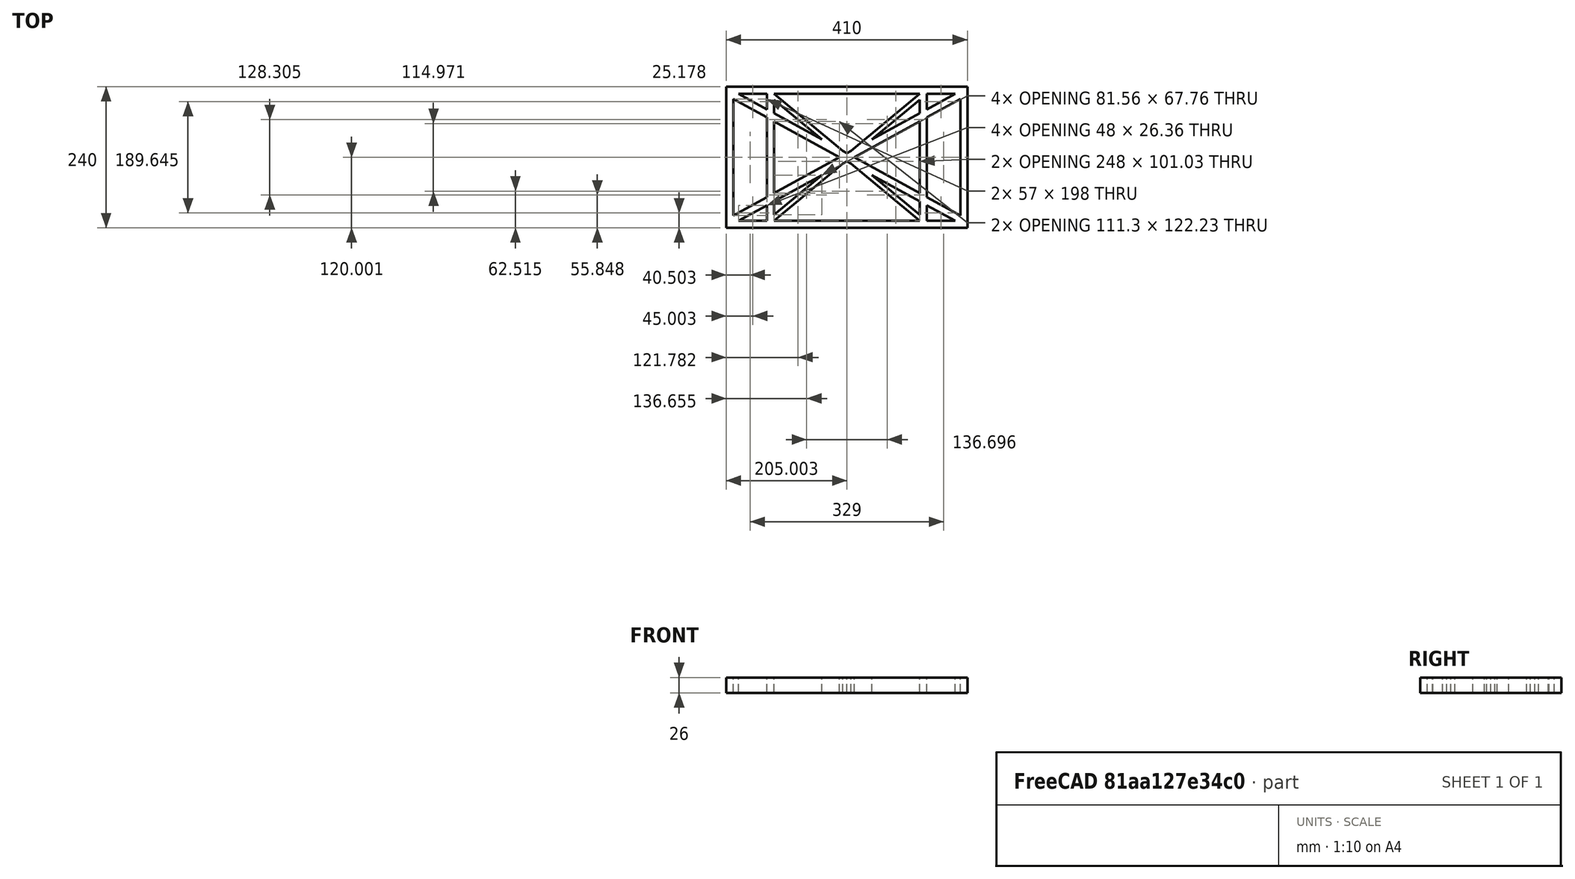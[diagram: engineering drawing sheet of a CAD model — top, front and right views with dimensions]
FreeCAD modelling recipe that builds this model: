
FCSTD DOCUMENT  (FreeCAD 0.19R0.19.2)
Label: laptopStand031
License: All rights reserved
LicenseURL: http://en.wikipedia.org/wiki/All_rights_reserved
objects: Sketcher::SketchObject×3, Part::Extrusion×1
note: 4 computed .brp shape members not serialized (recipe doc carries the construction recipe); baked Part::Feature solids carry a one-line shape summary decoded from their .brp

FEATURE [Sketcher::SketchObject] Sketch
  FullyConstrained = true
  sketch-geometry (52):
    g0: LineSegment StartX=-22.9272 StartY=136.221 StartZ=0 EndX=-22.9272 EndY=-103.779 EndZ=0
    g1: LineSegment StartX=-22.9272 StartY=136.221 StartZ=0 EndX=387.073 EndY=136.221 EndZ=0
    g2: LineSegment StartX=-22.9272 StartY=-103.779 StartZ=0 EndX=387.073 EndY=-103.779 EndZ=0
    g3: LineSegment StartX=387.073 StartY=136.221 StartZ=0 EndX=387.073 EndY=-103.779 EndZ=0
    g4: LineSegment StartX=375.073 StartY=115.221 StartZ=0 EndX=318.073 EndY=83.9235 EndZ=0
    g5: LineSegment StartX=-10.9272 StartY=-82.7794 StartZ=0 EndX=46.0728 EndY=-51.4823 EndZ=0
    g6: LineSegment StartX=-1.92719 StartY=124.221 StartZ=0 EndX=46.0728 EndY=97.8651 EndZ=0
    g7: LineSegment StartX=366.073 StartY=-91.7794 StartZ=0 EndX=318.073 EndY=-65.424 EndZ=0
    g8: LineSegment StartX=-10.9272 StartY=115.221 StartZ=0 EndX=-10.9272 EndY=-82.7794 EndZ=0
    g9: LineSegment StartX=375.073 StartY=-82.7794 StartZ=0 EndX=375.073 EndY=115.221 EndZ=0
    g10: LineSegment StartX=-1.92719 StartY=-91.7794 StartZ=0 EndX=46.0728 EndY=-91.7794 EndZ=0
    g11: LineSegment StartX=318.073 StartY=124.221 StartZ=0 EndX=366.073 EndY=124.221 EndZ=0
    g12: LineSegment StartX=306.073 StartY=-81.8102 StartZ=0 EndX=224.513 EndY=-14.0532 EndZ=0
    g13: LineSegment StartX=58.0728 StartY=114.251 StartZ=0 EndX=139.632 EndY=46.4944 EndZ=0
    g14: LineSegment StartX=306.073 StartY=124.221 StartZ=0 EndX=189.124 EndY=27.0628 EndZ=0
    g15: LineSegment StartX=58.0728 StartY=-91.7794 StartZ=0 EndX=175.022 EndY=5.37834 EndZ=0
    g16: LineSegment StartX=46.0728 StartY=124.221 StartZ=0 EndX=46.0728 EndY=97.8651 EndZ=0
    g17: LineSegment StartX=58.0728 StartY=-81.8102 StartZ=0 EndX=58.0728 EndY=-58.8351 EndZ=0
    g18: LineSegment StartX=318.073 StartY=124.221 StartZ=0 EndX=318.073 EndY=97.8651 EndZ=0
    g19: LineSegment StartX=306.073 StartY=114.251 StartZ=0 EndX=306.073 EndY=91.2763 EndZ=0
    g20: LineSegment StartX=182.073 StartY=23.1914 StartZ=0 EndX=189.124 EndY=27.0628 EndZ=0
    g21: LineSegment StartX=182.073 StartY=9.24976 StartZ=0 EndX=175.022 EndY=5.37834 EndZ=0
    g22: LineSegment StartX=224.513 StartY=46.4944 StartZ=0 EndX=306.073 EndY=114.251 EndZ=0
    g23: LineSegment StartX=175.022 StartY=27.0628 StartZ=0 EndX=58.0728 EndY=124.221 EndZ=0
    g24: LineSegment StartX=169.377 StartY=16.2206 StartZ=0 EndX=58.0728 EndY=77.3346 EndZ=0
    g25: LineSegment StartX=139.632 StartY=-14.0532 StartZ=0 EndX=58.0728 EndY=-81.8102 EndZ=0
    g26: LineSegment StartX=194.768 StartY=16.2206 StartZ=0 EndX=306.073 EndY=-44.8935 EndZ=0
    g27: LineSegment StartX=224.513 StartY=46.4944 StartZ=0 EndX=306.073 EndY=91.2763 EndZ=0
    g28: LineSegment StartX=175.022 StartY=27.0628 StartZ=0 EndX=182.073 EndY=23.1914 EndZ=0
    g29: LineSegment StartX=139.632 StartY=-14.0532 StartZ=0 EndX=58.0728 EndY=-58.8351 EndZ=0
    g30: LineSegment StartX=189.124 StartY=5.37834 StartZ=0 EndX=182.073 EndY=9.24976 EndZ=0
    g31: LineSegment StartX=189.124 StartY=5.37834 StartZ=0 EndX=306.073 EndY=-91.7794 EndZ=0
    g32: LineSegment StartX=306.073 StartY=77.3346 StartZ=0 EndX=306.073 EndY=-44.8935 EndZ=0
    g33: LineSegment StartX=318.073 StartY=83.9235 StartZ=0 EndX=318.073 EndY=-51.4823 EndZ=0
    g34: LineSegment StartX=318.073 StartY=97.8651 StartZ=0 EndX=366.073 EndY=124.221 EndZ=0
    g35: LineSegment StartX=306.073 StartY=77.3346 StartZ=0 EndX=194.768 EndY=16.2206 EndZ=0
    g36: LineSegment StartX=306.073 StartY=-58.8351 StartZ=0 EndX=224.513 EndY=-14.0532 EndZ=0
    g37: LineSegment StartX=306.073 StartY=-58.8351 StartZ=0 EndX=306.073 EndY=-81.8102 EndZ=0
    g38: LineSegment StartX=318.073 StartY=-51.4823 StartZ=0 EndX=375.073 EndY=-82.7794 EndZ=0
    g39: LineSegment StartX=318.073 StartY=-65.424 StartZ=0 EndX=318.073 EndY=-91.7794 EndZ=0
    g40: LineSegment StartX=306.073 StartY=124.221 StartZ=0 EndX=58.0728 EndY=124.221 EndZ=0
    g41: LineSegment StartX=318.073 StartY=-91.7794 StartZ=0 EndX=366.073 EndY=-91.7794 EndZ=0
    g42: LineSegment StartX=58.0728 StartY=-91.7794 StartZ=0 EndX=306.073 EndY=-91.7794 EndZ=0
    g43: LineSegment StartX=58.0728 StartY=-44.8935 StartZ=0 EndX=58.0728 EndY=77.3346 EndZ=0
    g44: LineSegment StartX=46.0728 StartY=-65.424 StartZ=0 EndX=-1.92719 EndY=-91.7794 EndZ=0
    g45: LineSegment StartX=46.0728 StartY=-65.424 StartZ=0 EndX=46.0728 EndY=-91.7794 EndZ=0
    g46: LineSegment StartX=58.0728 StartY=-44.8935 StartZ=0 EndX=169.377 EndY=16.2206 EndZ=0
    g47: LineSegment StartX=58.0728 StartY=91.2763 StartZ=0 EndX=58.0728 EndY=114.251 EndZ=0
    g48: LineSegment StartX=46.0728 StartY=83.9235 StartZ=0 EndX=46.0728 EndY=-51.4823 EndZ=0
    g49: LineSegment StartX=46.0728 StartY=124.221 StartZ=0 EndX=-1.92719 EndY=124.221 EndZ=0
    g50: LineSegment StartX=58.0728 StartY=91.2763 StartZ=0 EndX=139.632 EndY=46.4944 EndZ=0
    g51: LineSegment StartX=46.0728 StartY=83.9235 StartZ=0 EndX=-10.9272 EndY=115.221 EndZ=0
  constraints (102):
    c: Vertical(g0)
    c: Distance(g0) = 240
    c: Horizontal(g1)
    c: Distance(g1) = 410
    c: Coincident(g1,g0)
    c: Coincident(g2,g0)
    c: Horizontal(g2)
    c: Coincident(g3,g1)
    c: Vertical(g3)
    c: Coincident(g2,g3)
    c: Block(g1)
    c: Horizontal(g10)
    c: Horizontal(g11)
    c: PointOnObject(g35,g6)
    c: Coincident(g28,g20)
    c: Coincident(g30,g21)
    c: Tangent(g7,g24)
    c: PointOnObject(g24,g5)
    c: PointOnObject(g26,g4)
    c: Coincident(g20,g14)
    c: Tangent(g20,g27)
    c: Coincident(g50,g13)
    c: Coincident(g28,g23)
    c: Coincident(g22,g27)
    c: Coincident(g21,g15)
    c: Coincident(g29,g25)
    c: Tangent(g21,g29)
    c: Coincident(g36,g12)
    c: Coincident(g31,g30)
    c: Coincident(g22,g19)
    c: Tangent(g19,g32)
    c: Tangent(g18,g33)
    c: Coincident(g27,g19)
    c: Tangent(g27,g34)
    c: Coincident(g4,g33)
    c: Coincident(g35,g32)
    c: Tangent(g4,g35)
    c: Coincident(g37,g12)
    c: Tangent(g7,g36)
    c: Tangent(g32,g37)
    c: Coincident(g26,g32)
    c: Tangent(g26,g38)
    c: Coincident(g33,g38)
    c: Coincident(g39,g7)
    c: Tangent(g33,g39)
    c: Coincident(g25,g17)
    c: Tangent(g17,g43)
    c: Coincident(g29,g17)
    c: Tangent(g29,g44)
    c: Coincident(g45,g44)
    c: Tangent(g16,g45)
    c: Coincident(g5,g48)
    c: Coincident(g46,g43)
    c: Tangent(g5,g46)
    c: Tangent(g43,g47)
    c: Tangent(g16,g48)
    c: Coincident(g13,g47)
    c: PointOnObject(g40,g23)
    c: Tangent(g40,g49)
    c: Coincident(g6,g16)
    c: Coincident(g50,g47)
    c: Tangent(g6,g50)
    c: Coincident(g24,g43)
    c: Coincident(g51,g48)
    c: Tangent(g24,g51)
    c: Block(g23)
    c: Block(g14)
    c: Block(g20)
    c: Block(g40)
    c: Block(g18)
    c: Block(g34)
    c: Block(g4)
    c: Block(g38)
    c: Block(g9)
    c: Block(g36)
    c: Block(g37)
    c: Block(g7)
    c: Block(g39)
    c: Block(g22)
    c: Block(g31)
    c: Block(g42)
    c: Block(g21)
    c: Block(g15)
    c: Block(g29)
    c: Block(g25)
    c: Block(g45)
    c: Block(g44)
    c: Block(g5)
    c: Block(g8)
    c: Block(g51)
    c: Block(g6)
    c: Block(g16)
    c: Block(g13)
    c: Block(g47)
    c: Block(g35)
    c: Block(g32)
    c: Block(g24)
    c: Block(g46)
    c: Block(g49)
    c: Block(g11)
    c: Block(g41)
    c: Block(g10)
FEATURE [Part::Extrusion] Extrude
  Base = -> Sketch
  Dir = (0,0,1)
  DirMode = 2
  FaceMakerClass = Part::FaceMakerBullseye
  LengthFwd = 26
  LengthRev = 0
  Solid = true
  Symmetric = false
FEATURE [Sketcher::SketchObject] Sketch001
  FullyConstrained = true
  MapMode = 4
  Placement = pos=(0,0,0) rot=(0.57735,0.57735,0.57735;2.0944rad)
  Support = -> [Sketch]
  sketch-geometry (33):
    g0: LineSegment StartX=17.2232 StartY=-16.0875 StartZ=0 EndX=117.223 EndY=-16.0875 EndZ=0
    g1: LineSegment StartX=17.2232 StartY=-16.0875 StartZ=0 EndX=17.2232 EndY=-19.0875 EndZ=0
    g2: LineSegment StartX=117.223 StartY=-16.0875 StartZ=0 EndX=117.223 EndY=-19.0875 EndZ=0
    g3: BSplineCurve PolesCount=3 KnotsCount=2 Degree=2 IsPeriodic=0
    g4: LineSegment StartX=17.2232 StartY=-19.0875 StartZ=0 EndX=29.8094 EndY=-19.0875 EndZ=0
    g5: ArcOfCircle CenterX=73.122 CenterY=-32.2909 CenterZ=0 NormalX=0 NormalY=0 NormalZ=1 AngleXU=0 Radius=13 StartAngle=5.92268 EndAngle=9.06428
    g6: LineSegment StartX=85.2864 StartY=-36.8765 StartZ=0 EndX=78.9505 EndY=-53.7246 EndZ=0
    g7: LineSegment StartX=60.9577 StartY=-27.7052 StartZ=0 EndX=54.6191 EndY=-44.5532 EndZ=0
    g8: ArcOfCircle CenterX=66.7816 CenterY=-49.1439 CenterZ=0 NormalX=0 NormalY=0 NormalZ=1 AngleXU=0 Radius=13 StartAngle=2.78068 EndAngle=5.92131
    g9: ArcOfCircle CenterX=55.9263 CenterY=-78.1807 CenterZ=0 NormalX=0 NormalY=0 NormalZ=1 AngleXU=0 Radius=13 StartAngle=5.92268 EndAngle=9.06428
    g10: LineSegment StartX=68.0907 StartY=-82.7664 StartZ=0 EndX=61.7547 EndY=-99.6148 EndZ=0
    g11: ArcOfCircle CenterX=49.5884 CenterY=-95.0342 CenterZ=0 NormalX=0 NormalY=0 NormalZ=1 AngleXU=0 Radius=13 StartAngle=2.78068 EndAngle=5.92131
    g12: LineSegment StartX=43.7619 StartY=-73.595 StartZ=0 EndX=37.426 EndY=-90.4435 EndZ=0
    g13: ArcOfCircle CenterX=38.7206 CenterY=-124.067 CenterZ=0 NormalX=0 NormalY=0 NormalZ=1 AngleXU=0 Radius=13 StartAngle=5.92268 EndAngle=9.06428
    g14: LineSegment StartX=26.5562 StartY=-119.481 StartZ=0 EndX=20.2251 EndY=-136.329 EndZ=0
    g15: ArcOfCircle CenterX=32.3875 CenterY=-140.92 CenterZ=0 NormalX=0 NormalY=0 NormalZ=1 AngleXU=0 Radius=13 StartAngle=2.78068 EndAngle=5.92131
    g16: LineSegment StartX=50.885 StartY=-128.652 StartZ=0 EndX=44.549 EndY=-145.5 EndZ=0
    g17: ArcOfCircle CenterX=21.4715 CenterY=-169.934 CenterZ=0 NormalX=0 NormalY=0 NormalZ=1 AngleXU=0 Radius=13 StartAngle=5.92268 EndAngle=9.06428
    g18: LineSegment StartX=9.3071 StartY=-165.349 StartZ=0 EndX=2.97115 EndY=-182.197 EndZ=0
    g19: ArcOfCircle CenterX=15.1336 CenterY=-186.787 CenterZ=0 NormalX=0 NormalY=0 NormalZ=1 AngleXU=0 Radius=13 StartAngle=2.78068 EndAngle=5.92131
    g20: LineSegment StartX=33.6358 StartY=-174.52 StartZ=0 EndX=27.2999 EndY=-191.368 EndZ=0
    g21: LineSegment StartX=94.6577 StartY=-26.1351 StartZ=0 EndX=25.4551 EndY=-210.153 EndZ=0
    g22-g25: Circle x4 (B-spline internal-alignment scaffolding for g26; pole/knot coordinates omitted)
    g26: BSplineCurve PolesCount=4 KnotsCount=2 Degree=3 IsPeriodic=0
    g27: GeomPoint X=28.8094 Y=-19.0875 Z=0
    g28: GeomPoint X=47.0443 Y=-50.4712 Z=0
    g29: LineSegment StartX=47.3963 StartY=-49.5352 StartZ=0 EndX=-8.24091 EndY=-197.481 EndZ=0
    g30: Circle CenterX=53.5586 CenterY=-23.2695 CenterZ=0 NormalX=0 NormalY=0 NormalZ=1 AngleXU=0 Radius=3.24518
    g31: LineSegment StartX=25.4551 StartY=-210.153 StartZ=0 EndX=44.1752 EndY=-217.193 EndZ=0
    g32: LineSegment StartX=-8.24091 StartY=-197.481 StartZ=0 EndX=-195.441 EndY=-127.082 EndZ=0
  constraints (63):
    c: Horizontal(g0)
    c: Distance(g0) = 100
    c: Block(g0)
    c: Coincident(g1,g0)
    c: Vertical(g1)
    c: Distance(g1) = 3
    c: Coincident(g2,g0)
    c: Vertical(g2)
    c: Distance(g2) = 3
    c: Block(g3)
    c: Coincident(g3,g2)
    c: Coincident(g4,g1)
    c: Horizontal(g4)
    c: Block(g5)
    c: Distance(g6) = 18
    c: Coincident(g6,g5)
    c: Coincident(g7,g5)
    c: Block(g8)
    c: Coincident(g8,g7)
    c: Block(g7)
    c: Coincident(g10,g9)
    c: Coincident(g12,g9)
    c: Block(g11)
    c: Coincident(g11,g12)
    c: Block(g12)
    c: Block(g9)
    c: Block(g10)
    c: Coincident(g16,g13)
    c: Coincident(g14,g13)
    c: Block(g15)
    c: Coincident(g15,g14)
    c: Block(g14)
    c: Block(g13)
    c: Coincident(g20,g17)
    c: Coincident(g18,g17)
    c: Block(g19)
    c: Coincident(g19,g18)
    c: Block(g18)
    c: Block(g17)
    c: Distance(g20) = 18
    c: Block(g20)
    c: Block(g16)
    c: Coincident(g21,g3)
    c: Block(g21)
    c: Block(g6)
    c: Weight(g22) = 1
    c: Equal(g22,g23)
    c: Equal(g22,g24)
    c: Equal(g22,g25)
    c: InternalAlignment(g22-g25 -> g26) x4
    c: InternalAlignment(g27,g26)
    c: InternalAlignment(g28,g26)
    c: PointOnObject(g29,g25)
    c: PointOnObject(g4,g22)
    c: Block(g26)
    c: Block(g29)
    c: Block(g30)
    c: Distance(g31) = 20
    c: Perpendicular(g21,g31)
    c: Coincident(g31,g21)
    c: Coincident(g32,g29)
    c: Distance(g32) = 200
    c: Perpendicular(g32,g29)
FEATURE [Sketcher::SketchObject] Sketch002
  FullyConstrained = true
  Placement = pos=(0,0,0) rot=(-1,0,0;4.71239rad)
